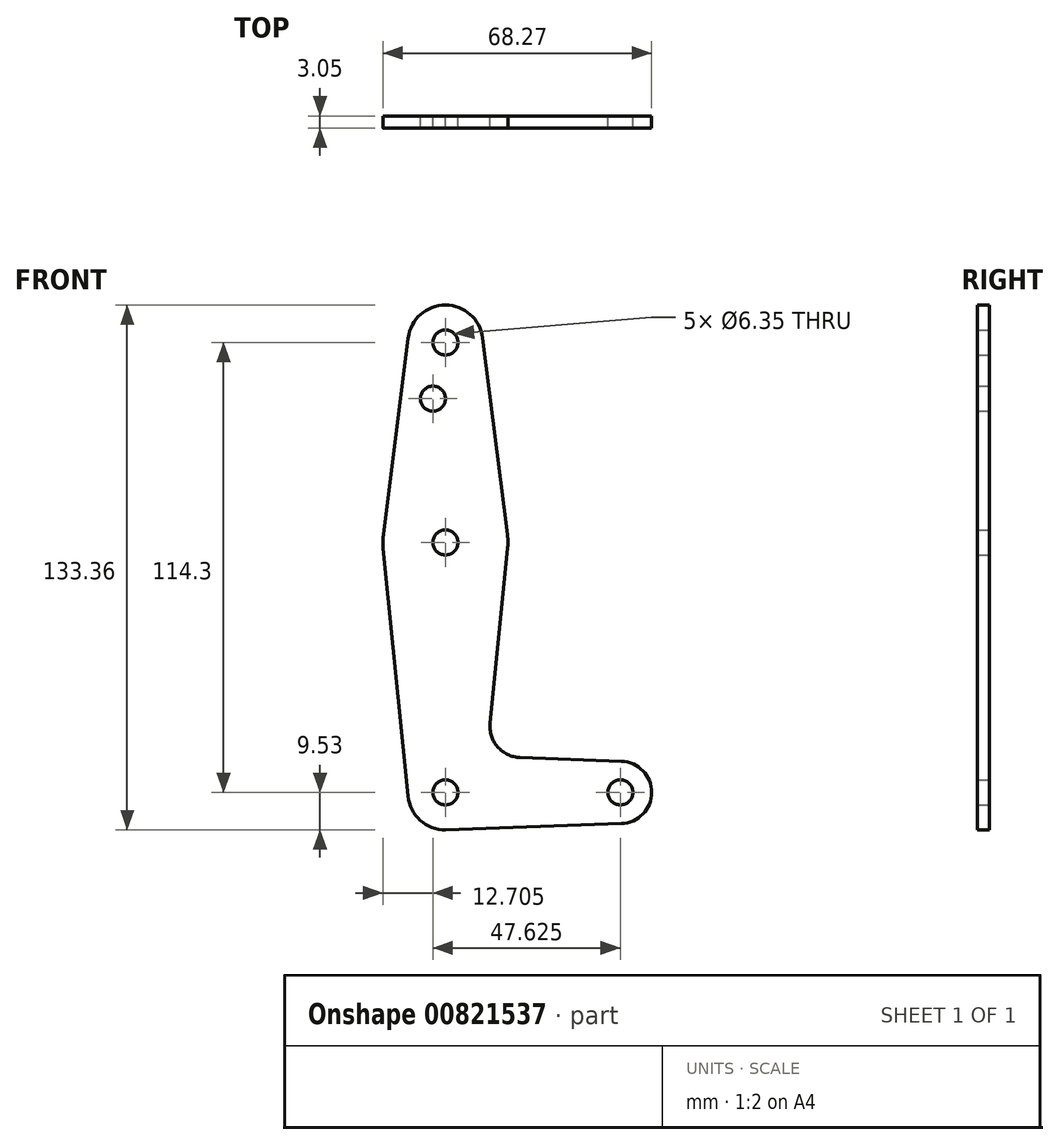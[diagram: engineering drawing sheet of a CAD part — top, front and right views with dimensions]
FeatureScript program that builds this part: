
annotation { "Feature Type Name" : "Feature", "Feature Type Description" : "" }
export const myFeature = defineFeature(function(context is Context, id is Id, definition is map)
    precondition{}
    {
        {
            var Q0;
            Q0=qCreatedBy(makeId("Front.planeOp"),FACE);
            var sketch = newSketch(context, id + "F0", { "sketchPlane" : qUnion([Q0])});
            skLineSegment(sketch, "E0", {"start": v(0, 114.3) * mm, "end": v(0, 0) * mm, "construction": true});
            skLineSegment(sketch, "E1", {"start": v(0, 0) * mm, "end": v(44.45, 0) * mm, "construction": true});
            skCircle(sketch, "E2", {"center": v(0, 114.3) * mm, "radius": 9.53 * mm});
            skCircle(sketch, "E3", {"center": v(0, 63.5) * mm, "radius": 15.88 * mm});
            skCircle(sketch, "E4", {"center": v(0, 0) * mm, "radius": 9.53 * mm});
            skCircle(sketch, "E5", {"center": v(44.45, 0) * mm, "radius": 7.94 * mm});
            skLineSegment(sketch, "E6", {"start": v(-9.48, -0.95) * mm, "end": v(-15.8, 61.91) * mm});
            skLineSegment(sketch, "E7", {"start": v(15.8, 61.91) * mm, "end": v(11.34, 17.6) * mm});
            skLineSegment(sketch, "E8", {"start": v(44.73, 7.93) * mm, "end": v(18.97, 8.85) * mm});
            skLineSegment(sketch, "E9", {"start": v(0, -9.53) * mm, "end": v(44.73, -7.93) * mm});
            skLineSegment(sketch, "E10", {"start": v(-9.45, 115.5) * mm, "end": v(-15.75, 65.48) * mm});
            skLineSegment(sketch, "E11", {"start": v(9.45, 115.5) * mm, "end": v(15.75, 65.48) * mm});
            skCircle(sketch, "E12", {"center": v(0, 114.3) * mm, "radius": 3.18 * mm});
            skCircle(sketch, "E13", {"center": v(0, 63.5) * mm, "radius": 3.18 * mm});
            skCircle(sketch, "E14", {"center": v(0, 0) * mm, "radius": 3.18 * mm});
            skCircle(sketch, "E15", {"center": v(44.45, 0) * mm, "radius": 3.18 * mm});
            skArc(sketch, "E16.filletArc", {"start": v(11.34, 17.6) * mm, "mid": v(13.26, 11.57) * mm, "end": v(18.97, 8.85) * mm});
            skCircle(sketch, "E17", {"center": v(-3.17, 100.03) * mm, "radius": 3.18 * mm});
            skSolve(sketch);
        }
        {
            var Q0;
            {var subQ1=sQuery(id+"F0.wireOp",EDGE,"E10");Q0=makeQuery(id+"F0.imprint","IMPRINT",FACE,{"disambiguationData":[TD([[makeQuery(id+"F0.imprint","IMPRINT",EDGE,{"derivedFrom":subQ1}),1.0]])]});}
            var Q1;
            Q1=makeQuery(id+"F0.imprint","IMPRINT",FACE,{"disambiguationData":[TD([[makeQuery(id+"F0.imprint","IMPRINT",EDGE,{"derivedFrom":sQuery(id+"F0.wireOp",EDGE,"E13")}),-1.0]])]});
            var Q2;
            {var subQ0=sQuery(id+"F0.wireOp",EDGE,"E6");Q2=makeQuery(id+"F0.imprint","IMPRINT",FACE,{"disambiguationData":[TD([[makeQuery(id+"F0.imprint","IMPRINT",EDGE,{"derivedFrom":subQ0}),-1.0]])]});}
            var Q3;
            Q3=makeQuery(id+"F0.imprint","IMPRINT",FACE,{"disambiguationData":[TD([[makeQuery(id+"F0.imprint","IMPRINT",EDGE,{"derivedFrom":sQuery(id+"F0.wireOp",EDGE,"E14")}),-1.0]])]});
            var Q4;
            Q4=makeQuery(id+"F0.imprint","IMPRINT",FACE,{"disambiguationData":[TD([[makeQuery(id+"F0.imprint","IMPRINT",EDGE,{"derivedFrom":sQuery(id+"F0.wireOp",EDGE,"E12")}),-1.0]])]});
            var Q5;
            Q5=makeQuery(id+"F0.imprint","IMPRINT",FACE,{"disambiguationData":[TD([[makeQuery(id+"F0.imprint","IMPRINT",EDGE,{"derivedFrom":sQuery(id+"F0.wireOp",EDGE,"E15")}),-1.0]])]});
            extrude(context, id + "F1", {"entities" : qUnion([Q0, Q1, Q2, Q3, Q4, Q5]), "depth" : 3.05 * mm, "offsetDistance" : 25.4 * mm});
        }
    });
